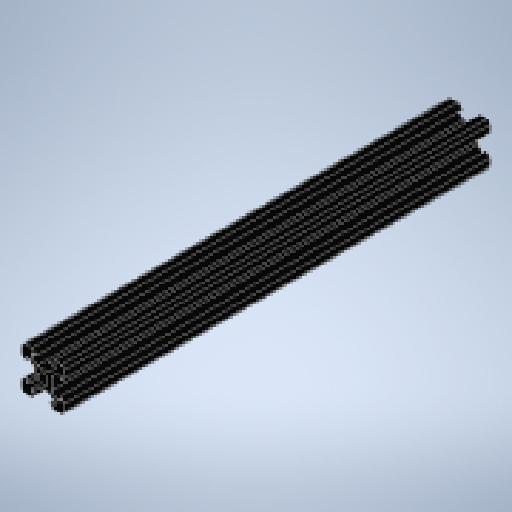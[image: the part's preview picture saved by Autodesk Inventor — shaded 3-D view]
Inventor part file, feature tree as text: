
AUTODESK INVENTOR PART (.ipt)
format: ipt  version: 2025.1 (Build 291241020, 241B)  size: 285,696 bytes
history: native  units: in
note: dims shown in document units (in); Inventor stores cm internally (conversion verified against a paired STEP export)
features: extrude x2, sketch x1, projected_geometry x1, other x1
ambient origin geometry x8: Origin, YZ Plane, XZ Plane, XY Plane, X Axis, Y Axis, Z Axis, Center Point
bodies: Solid1 (feature_tree)
feature tree (5):
  sketch  "Sketch1"  dims[d0=7.874in d1=0.0in d2=5.9055in d3=0.0in]
  extrude  "Extrusion1"  Depth=5.9055in TaperAngle=0.0deg
  extrude  "Extrusion2"  [1 undecoded]
  projected_geometry  "Projected Loop1"
  other  "Скругление1"
note: 1 required parameter value undecoded (feature->parameter linkage not recoverable at this tier; creation-order binding heuristic only, values carry confidence <= 0.55)
